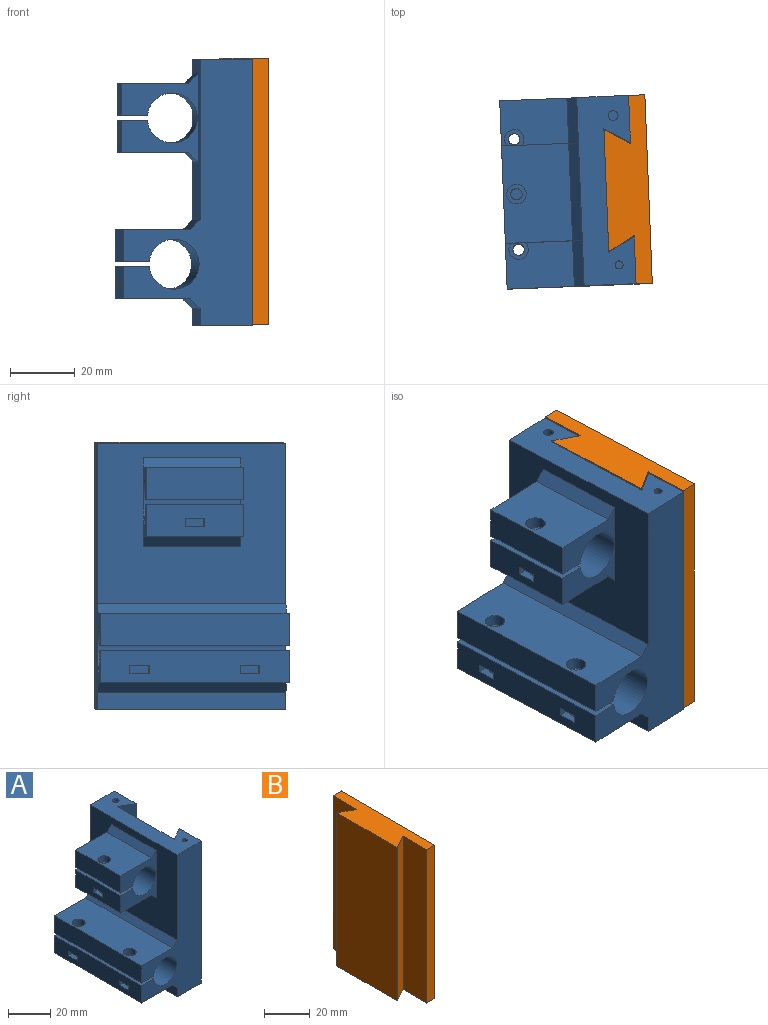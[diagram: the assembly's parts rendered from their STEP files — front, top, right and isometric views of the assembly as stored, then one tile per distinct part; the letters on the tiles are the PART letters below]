
ASSEMBLY  parts=2 mates=1
PART A: 77 faces, bbox 39.7x58x82 mm
  f0: plane 82x58mm, normal (1,0,0), area 2856.4mm2, adj f10,f12,f13,f14,f57,f59,f60,f61
  f1: plane 58x9.9mm, normal (-1,0,0), area 544.2mm2, adj f13,f14,f20,f21,f47,f48,f49,f50
  f2: cylinder r=1.75mm len=4.4mm, axis (0,0,1), area 48.4mm2, adj f20,f52
  f3: cylinder r=1.75mm len=4.4mm, axis (0,0,1), area 48.4mm2, adj f20,f47
  f4: cylinder r=1.75mm len=6.4mm, axis (0,0,1), area 70.4mm2, adj f18,f46
  f5: cylinder r=1.75mm len=6.4mm, axis (0,0,1), area 70.4mm2, adj f18,f44
  f6: cylinder r=1.75mm len=6.4mm, axis (0,0,1), area 70.4mm2, adj f26,f40
  f7: plane 30x9.9mm, normal (-1,0,0), area 282mm2, adj f28,f29,f31,f32,f34,f35,f36,f37
  f8: cylinder r=1.75mm len=4.4mm, axis (0,0,1), area 48.4mm2, adj f28,f34
  f9: plane 58x49.3mm, normal (-1,0,0), area 2037.4mm2, adj f10,f13,f14,f15,f23,f30,f31,f32
  f10: plane 58x16mm, normal (0,0,1), area 648.9mm2, adj f0,f9,f13,f14,f57,f58,f59,f73
  f11: plane 58x5.3mm, normal (-1,0,0), area 307.4mm2, adj f12,f13,f14,f22
  f12: plane 58x16mm, normal (0,0,-1), area 928mm2, adj f0,f11,f13,f14
  f13: plane 82x39.7mm, normal (0,-1,0), area 1629.1mm2, adj f0,f1,f9,f10,f11,f12,f15,f16
  f14: plane 82x39.7mm, normal (0,1,0), area 1629.1mm2, adj f0,f1,f9,f10,f11,f12,f15,f16
  f15: plane 58x3mm, normal (-0.71,0,0.71), area 246.1mm2, adj f9,f13,f14,f16
  f16: plane 58x20.7mm, normal (0,0,1), area 1144.1mm2, adj f13,f14,f15,f17,f43,f45
  f17: plane 58x9.9mm, normal (-1,0,0), area 574.2mm2, adj f13,f14,f16,f18
  f18: plane 58x8.04mm, normal (0,0,-1), area 447.2mm2, adj f4,f5,f13,f14,f17,f19
  f19: cylinder r=7.7mm len=58mm, axis (0,1,0), area 2713.1mm2, adj f13,f14,f18,f20
  f20: plane 58x8.04mm, normal (0,0,1), area 447.2mm2, adj f1,f2,f3,f13,f14,f19
  f21: plane 58x20.7mm, normal (0,0,-1), area 1181.4mm2, adj f1,f13,f14,f22,f41,f42
  f22: plane 58x3mm, normal (-0.71,0,-0.71), area 246.1mm2, adj f11,f13,f14,f21
  f23: plane 30x3mm, normal (-0.71,0,0.71), area 127.3mm2, adj f9,f24,f31,f32
  f24: plane 30x20.7mm, normal (0,0,1), area 592.7mm2, adj f23,f25,f31,f32,f39
  f25: plane 30x9.9mm, normal (-1,0,0), area 297mm2, adj f24,f26,f31,f32
  f26: plane 30x8.04mm, normal (0,0,-1), area 231.6mm2, adj f6,f25,f27,f31,f32
  f27: cylinder r=7.7mm len=30mm, axis (0,1,0), area 1403.3mm2, adj f26,f28,f31,f32
  f28: plane 30x8.04mm, normal (0,0,1), area 231.6mm2, adj f7,f8,f27,f31,f32
  f29: plane 30x20.7mm, normal (0,0,-1), area 611.4mm2, adj f7,f30,f31,f32,f33
  f30: plane 30x3mm, normal (-0.71,0,-0.71), area 127.3mm2, adj f9,f29,f31,f32
  f31: plane 27.4x23.7mm, normal (0,-1,0), area 317.1mm2, adj f7,f9,f23,f24,f25,f26,f27,f28
  f32: plane 27.4x23.7mm, normal (0,1,0), area 317.1mm2, adj f7,f9,f23,f24,f25,f26,f27,f28
  f33: cylinder r=1.75mm len=3.5mm, axis (0,0,1), area 33mm2, adj f29,f35
  f34: plane 7x6mm, normal (0,0,-1), area 32.4mm2, adj f7,f8,f36,f37,f38
  f35: plane 7x6mm, normal (0,0,1), area 32.4mm2, adj f7,f33,f36,f37,f38
  f36: plane 7x2.5mm, normal (0,-1,0), area 17.5mm2, adj f7,f34,f35,f38
  f37: plane 7x2.5mm, normal (0,1,0), area 17.5mm2, adj f7,f34,f35,f38
  f38: plane 6x2.5mm, normal (-1,0,0), area 15mm2, adj f34,f35,f36,f37
  f39: cylinder r=3mm len=6mm, axis (0,0,1), area 66mm2, adj f24,f40
  f40: plane 6x6mm, normal (0,0,1), area 18.7mm2, adj f6,f39
  f41: cylinder r=1.75mm len=3.5mm, axis (0,0,1), area 33mm2, adj f21,f53
  f42: cylinder r=1.75mm len=3.5mm, axis (0,0,1), area 33mm2, adj f21,f48
  f43: cylinder r=3mm len=6mm, axis (0,0,1), area 66mm2, adj f16,f44
  f44: plane 6x6mm, normal (0,0,1), area 18.7mm2, adj f5,f43
  f45: cylinder r=3mm len=6mm, axis (0,0,1), area 66mm2, adj f16,f46
  f46: plane 6x6mm, normal (0,0,1), area 18.7mm2, adj f4,f45
  f47: plane 7x6mm, normal (0,0,-1), area 32.4mm2, adj f1,f3,f49,f50,f51
  f48: plane 7x6mm, normal (0,0,1), area 32.4mm2, adj f1,f42,f49,f50,f51
  f49: plane 7x2.5mm, normal (0,-1,0), area 17.5mm2, adj f1,f47,f48,f51
  f50: plane 7x2.5mm, normal (0,1,0), area 17.5mm2, adj f1,f47,f48,f51
  f51: plane 6x2.5mm, normal (-1,0,0), area 15mm2, adj f47,f48,f49,f50
  f52: plane 7x6mm, normal (0,0,-1), area 32.4mm2, adj f1,f2,f54,f55,f56
  f53: plane 7x6mm, normal (0,0,1), area 32.4mm2, adj f1,f41,f54,f55,f56
  f54: plane 7x2.5mm, normal (0,-1,0), area 17.5mm2, adj f1,f52,f53,f56
  f55: plane 7x2.5mm, normal (0,1,0), area 17.5mm2, adj f1,f52,f53,f56
  f56: plane 6x2.5mm, normal (-1,0,0), area 15mm2, adj f52,f53,f54,f55
  f57: plane 65x8mm, normal (-0.5,-0.87,0), area 600.4mm2, adj f0,f10,f58,f60
  f58: plane 65x38mm, normal (1,0,0), area 2470mm2, adj f10,f57,f59,f60
  f59: plane 65x8mm, normal (-0.5,0.87,0), area 600.4mm2, adj f0,f10,f58,f60
  f60: plane 38x8mm, normal (0,0,1), area 267mm2, adj f0,f57,f58,f59
  f61: plane 8x6mm, normal (0,0,-1), area 40.8mm2, adj f0,f62,f64,f65,f76
  f62: plane 8x2.5mm, normal (0,1,0), area 20mm2, adj f0,f61,f63,f65
  f63: plane 8x6mm, normal (0,0,1), area 40.8mm2, adj f0,f62,f64,f65,f75
  f64: plane 8x2.5mm, normal (0,-1,0), area 20mm2, adj f0,f61,f63,f65
  f65: plane 6x2.5mm, normal (1,0,0), area 15mm2, adj f61,f62,f63,f64
  f66: plane 8x6mm, normal (0,0,-1), area 43.2mm2, adj f0,f67,f69,f70,f73
  f67: plane 8x2.5mm, normal (0,1,0), area 20mm2, adj f0,f66,f68,f70
  f68: plane 8x6mm, normal (0,0,1), area 43.2mm2, adj f0,f67,f69,f70,f72
  f69: plane 8x2.5mm, normal (0,-1,0), area 20mm2, adj f0,f66,f68,f70
  f70: plane 6x2.5mm, normal (1,0,0), area 15mm2, adj f66,f67,f68,f69
  f71: plane 2.48x2.48mm, normal (0,0,1), area 4.8mm2, adj f72
  f72: cylinder r=1.24mm len=9.5mm, axis (0,0,1), area 73.9mm2, adj f68,f71
  f73: cylinder r=1.24mm len=8mm, axis (0,0,1), area 62.3mm2, adj f10,f66
  f74: plane 3.04x3.04mm, normal (0,0,1), area 7.2mm2, adj f75
  f75: cylinder r=1.52mm len=9.5mm, axis (0,0,1), area 90.6mm2, adj f63,f74
  f76: cylinder r=1.52mm len=8mm, axis (0,0,1), area 76.3mm2, adj f10,f61
PART B: 12 faces, bbox 13x58x82 mm
  f0: plane 82x14.7mm, normal (-1,0,0), area 1205.7mm2, adj f1,f9,f10,f11
  f1: plane 82x0.2mm, normal (0,1,0), area 16.4mm2, adj f0,f2,f10,f11
  f2: plane 82x7.8mm, normal (0.5,0.87,0), area 738.5mm2, adj f1,f3,f10,f11
  f3: plane 82x37.6mm, normal (-1,0,0), area 3083.2mm2, adj f2,f4,f10,f11
  f4: plane 82x7.8mm, normal (0.5,-0.87,0), area 738.5mm2, adj f3,f5,f10,f11
  f5: plane 82x0.2mm, normal (0,-1,0), area 16.4mm2, adj f4,f6,f10,f11
  f6: plane 82x14.7mm, normal (-1,0,0), area 1205.7mm2, adj f5,f7,f10,f11
  f7: plane 82x5mm, normal (0,-1,0), area 410mm2, adj f6,f8,f10,f11
  f8: plane 82x58mm, normal (1,0,0), area 4756mm2, adj f7,f9,f10,f11
  f9: plane 82x5mm, normal (0,1,0), area 410mm2, adj f0,f8,f10,f11
  f10: plane 58x13mm, normal (0,0,1), area 553.9mm2, adj f0,f1,f2,f3,f4,f5,f6,f7
  f11: plane 58x13mm, normal (0,0,-1), area 553.9mm2, adj f0,f1,f2,f3,f4,f5,f6,f7
PLACE A rot(axis=(0,0,1),2.3deg) t=(-38.4,-12.06,-9.26)mm
PLACE B rot(axis=(0,0,1),2.3deg) t=(-22.41,-11.43,-8.83)mm
MATE slider B.f10 <-> A.f10  axis (0,0,1) through (-21.26,-40.4,73.17)mm
